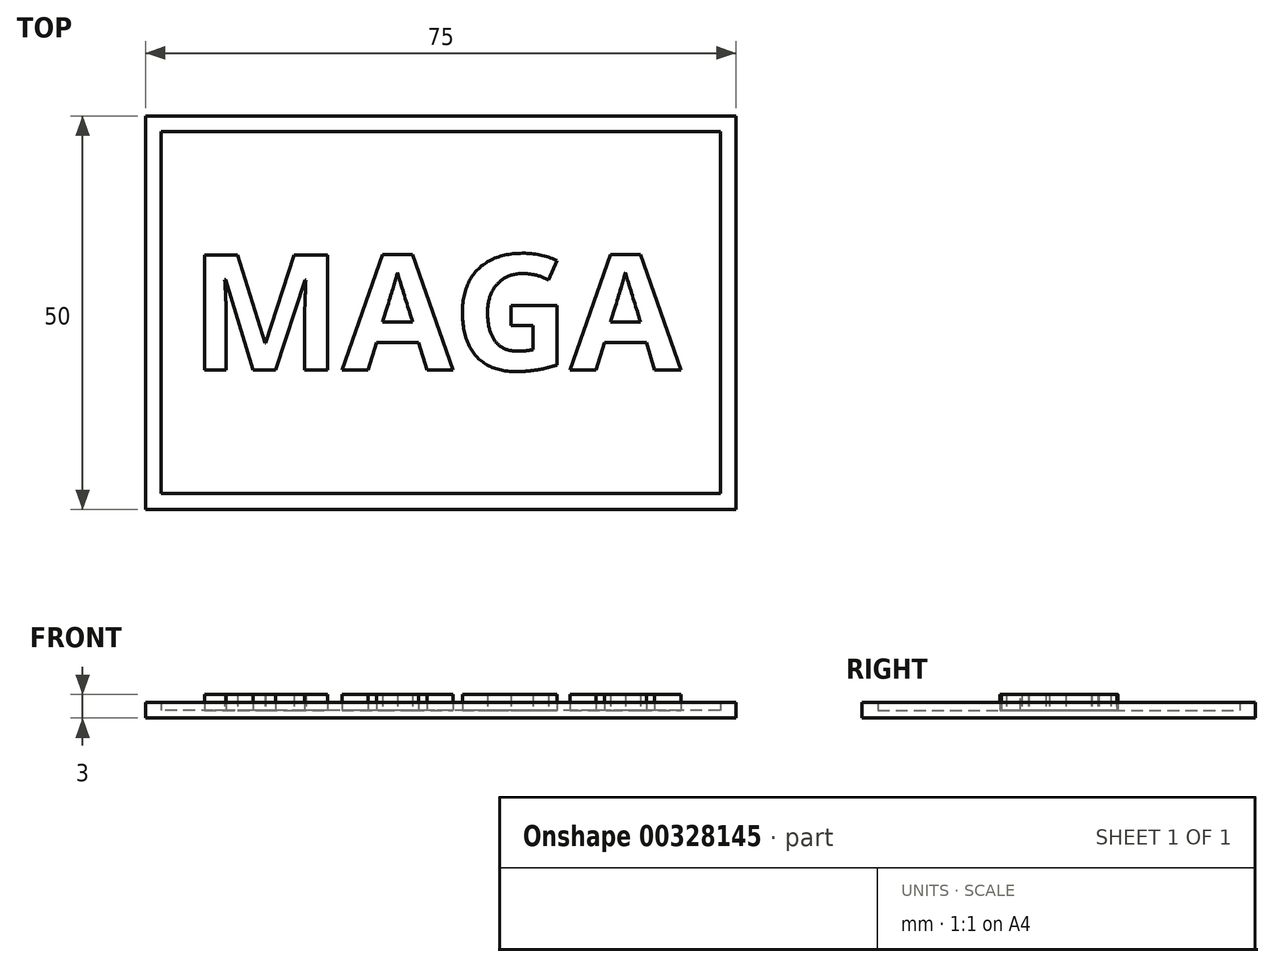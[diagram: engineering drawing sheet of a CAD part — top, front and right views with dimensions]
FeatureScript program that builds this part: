
annotation { "Feature Type Name" : "Feature", "Feature Type Description" : "" }
export const myFeature = defineFeature(function(context is Context, id is Id, definition is map)
    precondition{}
    {
        {
            var Q0;
            Q0=qCreatedBy(makeId("Top.planeOp"),FACE);
            var sketch = newSketch(context, id + "F0", { "sketchPlane" : qUnion([Q0])});
            skLineSegment(sketch, "E0.bottom", {"start": v(37.5, -25) * mm, "end": v(-37.5, -25) * mm});
            skLineSegment(sketch, "E0.top", {"start": v(37.5, 25) * mm, "end": v(-37.5, 25) * mm});
            skLineSegment(sketch, "E0.left", {"start": v(37.5, -25) * mm, "end": v(37.5, 25) * mm});
            skLineSegment(sketch, "E0.right", {"start": v(-37.5, -25) * mm, "end": v(-37.5, 25) * mm});
            skPoint(sketch, "E0.middle", {"position": v(0, 0) * mm});
            skLineSegment(sketch, "E1.bottom", {"start": v(35.5, -23) * mm, "end": v(-35.5, -23) * mm});
            skLineSegment(sketch, "E1.top", {"start": v(35.5, 23) * mm, "end": v(-35.5, 23) * mm});
            skLineSegment(sketch, "E1.left", {"start": v(35.5, -23) * mm, "end": v(35.5, 23) * mm});
            skLineSegment(sketch, "E1.right", {"start": v(-35.5, -23) * mm, "end": v(-35.5, 23) * mm});
            skSolve(sketch);
        }
        {
            var Q0;
            Q0=makeQuery(id+"F0.imprint","IMPRINT",FACE,{"disambiguationData":[TD([[makeQuery(id+"F0.imprint","IMPRINT",EDGE,{"derivedFrom":sQuery(id+"F0.wireOp",EDGE,"E0.bottom")}),-1.0]])]});
            var Q1;
            Q1=makeQuery(id+"F0.imprint","IMPRINT",FACE,{"disambiguationData":[TD([[makeQuery(id+"F0.imprint","IMPRINT",EDGE,{"derivedFrom":sQuery(id+"F0.wireOp",EDGE,"E1.bottom")}),-1.0]])]});
            extrude(context, id + "F1", {"entities" : qUnion([Q0, Q1]), "oppositeDirection" : true, "depth" : 1 * mm});
        }
        {
            var Q0;
            Q0=makeQuery(id+"F0.imprint","IMPRINT",FACE,{"disambiguationData":[TD([[makeQuery(id+"F0.imprint","IMPRINT",EDGE,{"derivedFrom":sQuery(id+"F0.wireOp",EDGE,"E0.bottom")}),-1.0]])]});
            extrude(context, id + "F2", {"entities" : qUnion([Q0]), "operationType" : NewBodyOperationType.ADD, "depth" : 1 * mm});
        }
        {
            var Q0;
            Q0=makeQuery(id+"F1.opExtrude","CAP_FACE",FACE,{"disambiguationData":[OSD([sQuery(id+"F0.wireOp",EDGE,"E0.bottom"),sQuery(id+"F0.wireOp",EDGE,"E0.top"),sQuery(id+"F0.wireOp",EDGE,"E0.left"),sQuery(id+"F0.wireOp",EDGE,"E0.right")])],"isStart":true});
            var sketch = newSketch(context, id + "F3", { "sketchPlane" : qUnion([Q0])});
            skText(sketch, "E2", { "text": "MAGA", "fontName": "OpenSans-Bold.ttf"});
            skLineSegment(sketch, "E3", {"start": v(0, 0) * mm, "end": v(0, 23) * mm, "construction": true});
            const initialGuessF3  = {"E2": [-0.03186, -0.00728, 1, 0, 0.01474]};
            skSetInitialGuess(sketch, initialGuessF3);
            skSolve(sketch);
        }
        {
            var Q0;
            Q0 = qSketchRegion(id + "F3", true);
            extrude(context, id + "F4", {"entities" : qUnion([Q0]), "operationType" : NewBodyOperationType.ADD, "depth" : 2 * mm});
        }
    });
